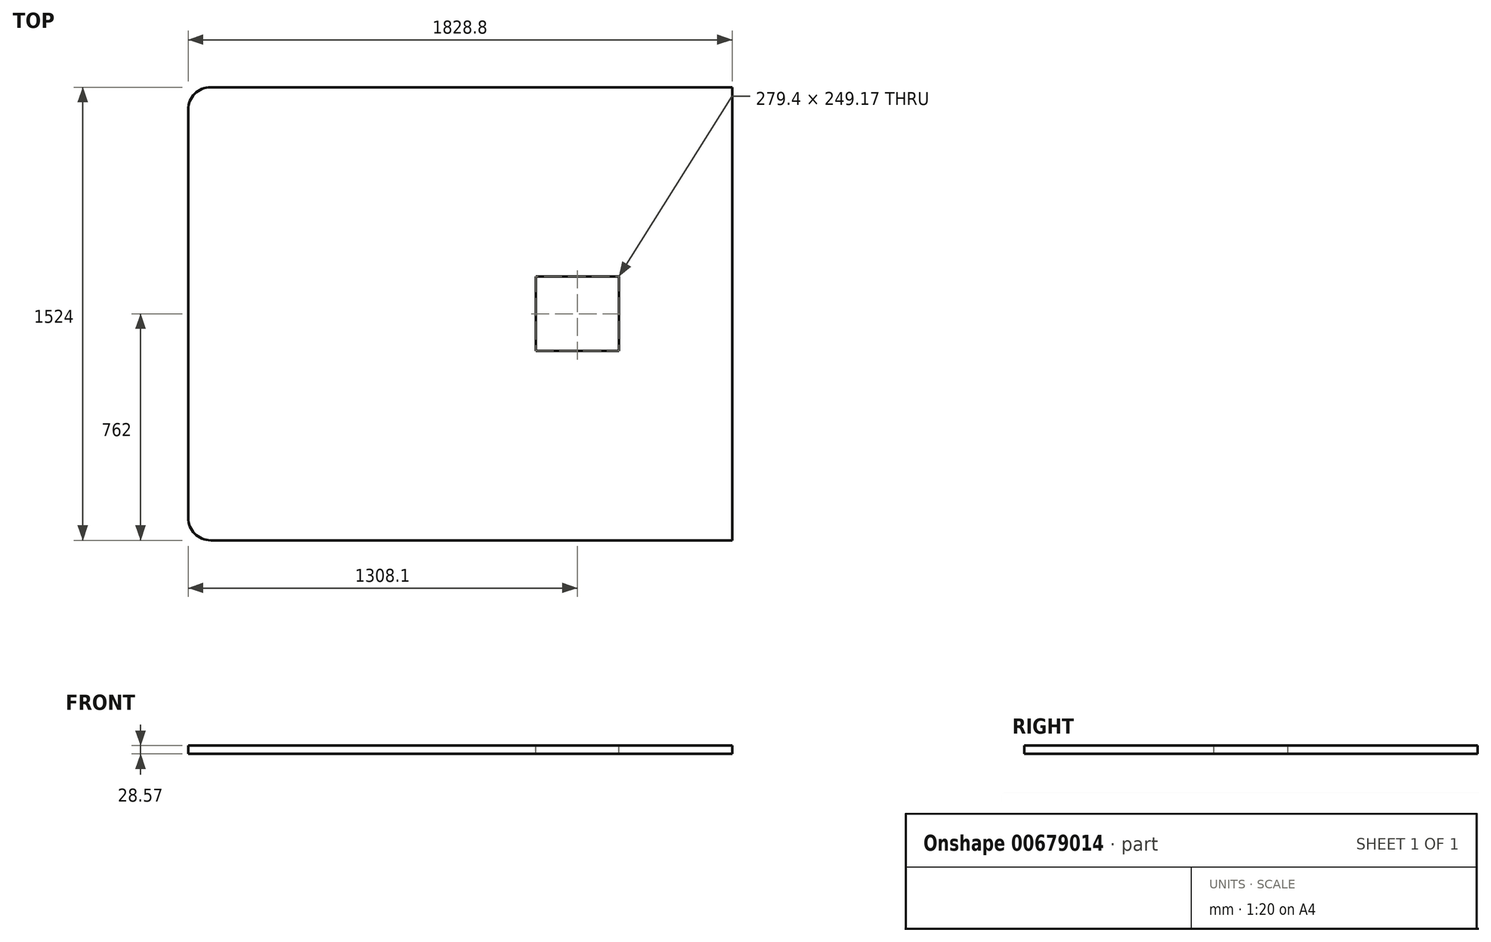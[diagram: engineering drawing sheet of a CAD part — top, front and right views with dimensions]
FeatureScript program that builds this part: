
annotation { "Feature Type Name" : "Feature", "Feature Type Description" : "" }
export const myFeature = defineFeature(function(context is Context, id is Id, definition is map)
    precondition{}
    {
        {
            var Q0;
            Q0=qCreatedBy(makeId("Top.planeOp"),FACE);
            var sketch = newSketch(context, id + "F0", { "sketchPlane" : qUnion([Q0])});
            skLineSegment(sketch, "E0.bottom", {"start": v(914.4, 762) * mm, "end": v(-838.2, 762) * mm});
            skLineSegment(sketch, "E0.top", {"start": v(914.4, -762) * mm, "end": v(-838.2, -762) * mm});
            skLineSegment(sketch, "E0.left", {"start": v(914.4, 762) * mm, "end": v(914.4, -762) * mm});
            skLineSegment(sketch, "E0.right", {"start": v(-914.4, 685.8) * mm, "end": v(-914.4, -685.8) * mm});
            skPoint(sketch, "E0.middle", {"position": v(0, 0) * mm});
            skPoint(sketch, "E1.visualSharp", {"position": v(-914.4, -762) * mm});
            skArc(sketch, "E1.filletArc", {"start": v(-914.4, -685.8) * mm, "mid": v(-892.08, -739.68) * mm, "end": v(-838.2, -762) * mm});
            skPoint(sketch, "E2.visualSharp", {"position": v(-914.4, 762) * mm});
            skArc(sketch, "E2.filletArc", {"start": v(-838.2, 762) * mm, "mid": v(-892.08, 739.68) * mm, "end": v(-914.4, 685.8) * mm});
            skSolve(sketch);
        }
        {
            var Q0;
            Q0=makeQuery(id+"F0.imprint","IMPRINT",FACE,{"disambiguationData":[TD([[makeQuery(id+"F0.imprint","IMPRINT",EDGE,{"derivedFrom":sQuery(id+"F0.wireOp",EDGE,"E0.bottom")}),1.0]])]});
            extrude(context, id + "F1", {"entities" : qUnion([Q0]), "depth" : 28.57 * mm, "offsetDistance" : 25.4 * mm});
        }
        {
            var Q0;
            Q0=makeQuery(id+"F1.opExtrude","CAP_FACE",FACE,{"disambiguationData":[OSD([sQuery(id+"F0.wireOp",EDGE,"E0.bottom"),sQuery(id+"F0.wireOp",EDGE,"E0.top"),sQuery(id+"F0.wireOp",EDGE,"E0.left"),sQuery(id+"F0.wireOp",EDGE,"E0.right"),sQuery(id+"F0.wireOp",EDGE,"E1.filletArc"),sQuery(id+"F0.wireOp",EDGE,"E2.filletArc")])],"isStart":false});
            var sketch = newSketch(context, id + "F2", { "sketchPlane" : qUnion([Q0])});
            skLineSegment(sketch, "E3", {"start": v(914.4, 0) * mm, "end": v(533.4, 0) * mm});
            skLineSegment(sketch, "E4", {"start": v(533.4, 0) * mm, "end": v(393.7, 0) * mm});
            skLineSegment(sketch, "E5.bottom", {"start": v(533.4, 124.59) * mm, "end": v(254, 124.59) * mm});
            skLineSegment(sketch, "E5.top", {"start": v(533.4, -124.59) * mm, "end": v(254, -124.59) * mm});
            skLineSegment(sketch, "E5.left", {"start": v(533.4, 124.59) * mm, "end": v(533.4, -124.59) * mm});
            skLineSegment(sketch, "E5.right", {"start": v(254, 124.59) * mm, "end": v(254, -124.59) * mm});
            skPoint(sketch, "E5.middle", {"position": v(393.7, 0) * mm});
            skSolve(sketch);
        }
        {
            var Q0;
            {var subQ3=sQuery(id+"F2.wireOp",EDGE,"E5.bottom");Q0=makeQuery(id+"F2.imprint","IMPRINT",FACE,{"disambiguationData":[TD([[makeQuery(id+"F2.imprint","IMPRINT",EDGE,{"derivedFrom":subQ3}),1.0]])]});}
            extrude(context, id + "F3", {"entities" : qUnion([Q0]), "operationType" : NewBodyOperationType.REMOVE, "oppositeDirection" : true, "depth" : 28.57 * mm, "offsetDistance" : 25.4 * mm});
        }
    });
